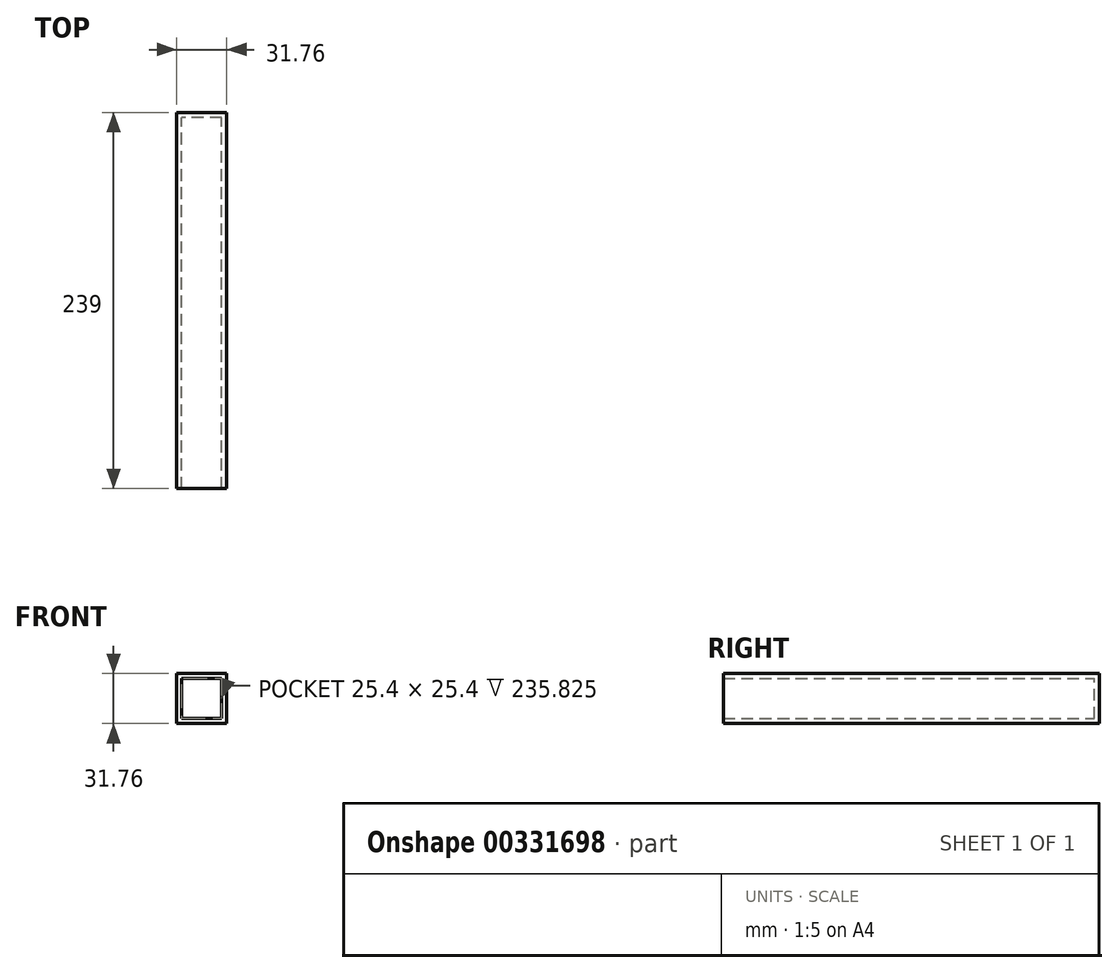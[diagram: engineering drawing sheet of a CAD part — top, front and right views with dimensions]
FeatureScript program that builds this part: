
annotation { "Feature Type Name" : "Feature", "Feature Type Description" : "" }
export const myFeature = defineFeature(function(context is Context, id is Id, definition is map)
    precondition{}
    {
        {
            var Q0;
            Q0=qCreatedBy(makeId("Front.planeOp"),FACE);
            var sketch = newSketch(context, id + "F0", { "sketchPlane" : qUnion([Q0])});
            skLineSegment(sketch, "E0.bottom", {"start": v(15.88, -15.87) * mm, "end": v(-15.88, -15.88) * mm});
            skLineSegment(sketch, "E0.top", {"start": v(15.88, 15.88) * mm, "end": v(-15.88, 15.87) * mm});
            skLineSegment(sketch, "E0.left", {"start": v(15.88, -15.88) * mm, "end": v(15.88, 15.88) * mm});
            skLineSegment(sketch, "E0.right", {"start": v(-15.88, -15.88) * mm, "end": v(-15.88, 15.88) * mm});
            skPoint(sketch, "E0.middle", {"position": v(0, 0) * mm});
            skSolve(sketch);
        }
        {
            var Q0;
            Q0=makeQuery(id+"F0.imprint","IMPRINT",FACE,{"disambiguationData":[TD([[makeQuery(id+"F0.imprint","IMPRINT",EDGE,{"derivedFrom":sQuery(id+"F0.wireOp",EDGE,"E0.bottom")}),-1.0]])]});
            extrude(context, id + "F1", {"entities" : qUnion([Q0]), "endBound" : BoundingType.SYMMETRIC, "depth" : 239 * mm});
        }
        {
            var Q0;
            Q0=makeQuery(id+"F1.opExtrude","CAP_FACE",FACE,{"disambiguationData":[OSD([sQuery(id+"F0.wireOp",EDGE,"E0.bottom"),sQuery(id+"F0.wireOp",EDGE,"E0.top"),sQuery(id+"F0.wireOp",EDGE,"E0.left"),sQuery(id+"F0.wireOp",EDGE,"E0.right")])],"isStart":false});
            shell(context, id + "F2", {"entities" : qUnion([Q0]), "thickness" : 3.17 * mm});
        }
    });
